# Revit family: Rahmenkassette Schwerlast, blind, RKSL, Nenngröße 250-3, Belastungsklasse 2
name_source: partatom
category: Generic Models
revit_build: Autodesk Revit 2015 (Build: 20140606_1530(x64)
units: mm (PartAtom-declared; Revit-internal decimal feet)

## types (4) — shared parameters
Cut depth = 9 mm  [stored 0.0295276 ft]
Manufacturer = OBO Bettermann
Material = Stainless Steel
URL = http://www.obo-bettermann.com
Width = 324 mm  [stored 1.06299 ft]
Width 1 = 288 mm  [stored 0.944882 ft]

## per-type parameters (varying)
| type | GTIN | Height | Height 1 | Manufacturer Art.No. |
| RK SL2 V2 20 | 4012195105961 | 20 mm  [stored 0.0656168 ft] | 18 mm  [stored 0.0590551 ft] | 7405932 |
| RK SL2 V2 25 | 4012195105992 | 25 mm  [stored 0.082021 ft] | 23 mm  [stored 0.0754593 ft] | 7405936 |
| RK SL2 V2 30 | 4012195106005 | 30 mm  [stored 0.0984252 ft] | 28 mm  [stored 0.0918635 ft] | 7405940 |
| RK SL2 V2 40 | 4012195106029 | 40 mm  [stored 0.131234 ft] | 38 mm  [stored 0.124672 ft] | 7405948 |

note: column(s) folded — value = type name in every type: Article Type

note: [stored X ft] marks values corroborated as IEEE doubles in the binary element streams (Revit-internal decimal feet)

## geometry (parser evidence)
native form markers: Sweep x2
no freeform markers — native parametric forms only
